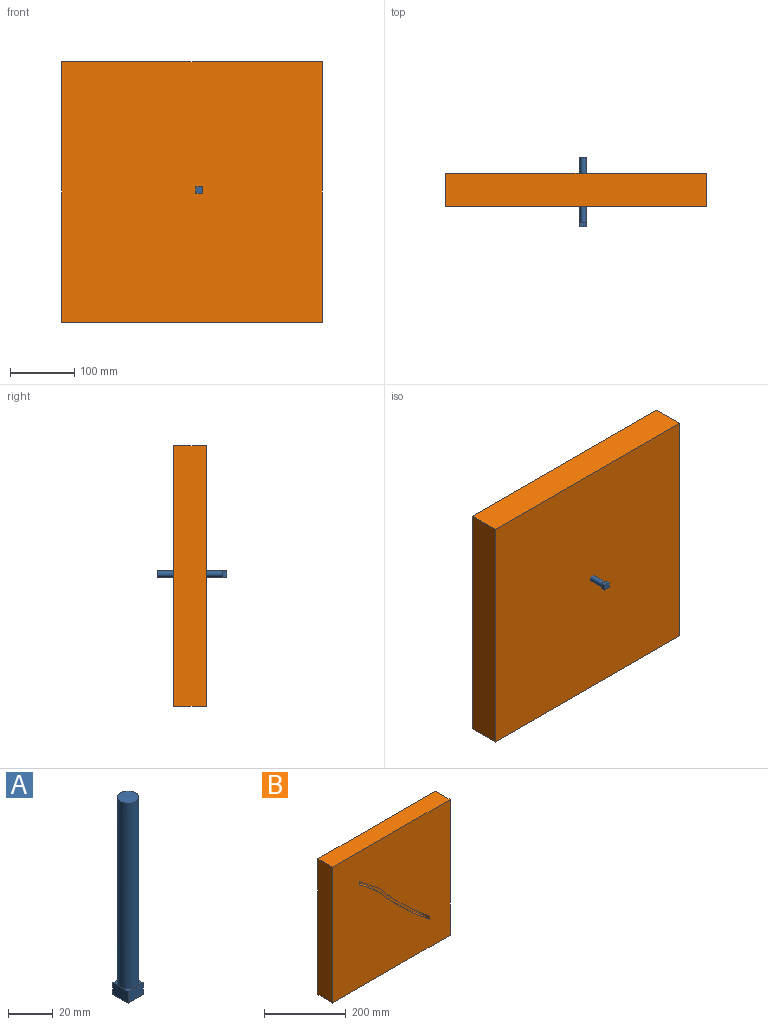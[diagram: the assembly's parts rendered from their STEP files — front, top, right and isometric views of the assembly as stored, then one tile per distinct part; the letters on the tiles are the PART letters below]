
ASSEMBLY  parts=2 mates=2
PART A: 11 faces, bbox 9.5x9.5x108 mm
  f0: cylinder r=4.76mm len=101.6mm, axis (0,0,-1), area 3040.2mm2, adj f1,f2,f3,f4,f5
  f1: plane 9.53x9.53mm, normal (0,0,1), area 71.3mm2, adj f0
  f2: plane 4.76x4.76mm, normal (0,0,1), area 4.9mm2, adj f0,f6,f9
  f3: plane 4.76x4.76mm, normal (0,0,1), area 4.9mm2, adj f0,f6,f7
  f4: plane 4.76x4.76mm, normal (0,0,1), area 4.9mm2, adj f0,f7,f8
  f5: plane 4.76x4.76mm, normal (0,0,1), area 4.9mm2, adj f0,f8,f9
  f6: plane 9.53x6.35mm, normal (0,1,0), area 60.5mm2, adj f2,f3,f7,f9,f10
  f7: plane 9.53x6.35mm, normal (-1,0,0), area 60.5mm2, adj f3,f4,f6,f8,f10
  f8: plane 9.53x6.35mm, normal (0,-1,0), area 60.5mm2, adj f4,f5,f7,f9,f10
  f9: plane 9.53x6.35mm, normal (1,0,0), area 60.5mm2, adj f2,f5,f6,f8,f10
  f10: plane 9.53x9.53mm, normal (0,0,-1), area 90.7mm2, adj f6,f7,f8,f9
PART B: 11 faces, bbox 428.3x98.1x428.3 mm
  f0: plane 406.4x50.8mm, normal (-1,0,0), area 20645.1mm2, adj f1,f3,f4,f5
  f1: plane 406.4x50.8mm, normal (0,0,-1), area 20645.1mm2, adj f0,f2,f4,f5
  f2: plane 406.4x50.8mm, normal (1,0,0), area 20645.1mm2, adj f1,f3,f4,f5
  f3: plane 406.4x50.8mm, normal (0,0,1), area 20645.1mm2, adj f0,f2,f4,f5
  f4: plane 406.4x406.4mm, normal (0,1,0), area 165161mm2, adj f0,f1,f2,f3
  f5: plane 428.25x428.25mm, normal (0,-1,0), area 162628.8mm2, adj f0,f1,f2,f3,f6,f7,f8,f10
  f6: plane 25.4x9.64mm, normal (1,0,0.05), area 245.2mm2, adj f5,f8,f9,f10
  f7: plane 25.4x9.65mm, normal (-1,0,0), area 245.2mm2, adj f5,f8,f9,f10
  f8: bspline ~241.64x224.33mm, area 8396.4mm2, adj f5,f6,f7,f9
  f9: plane 244.6x236.49mm, normal (0,-1,0), area 2049.9mm2, adj f6,f7,f8,f10
  f10: bspline ~242.07x224.32mm, area 8404.9mm2, adj f5,f6,f7,f9
PLACE A rot(axis=(-1,0,0),90deg) t=(214.18,-25.4,-200.08)mm
PLACE B rot(axis=(1,0,0),180deg) t=(0,50.8,0)mm
MATE slider A.f0 <-> B.f9  axis (0,-1,0) through (214.18,-31.75,-200.08)mm
MATE pin_slot A.f0 <-> B.f9  axis (0,-1,0) through (214.18,25.4,-200.08)mm
